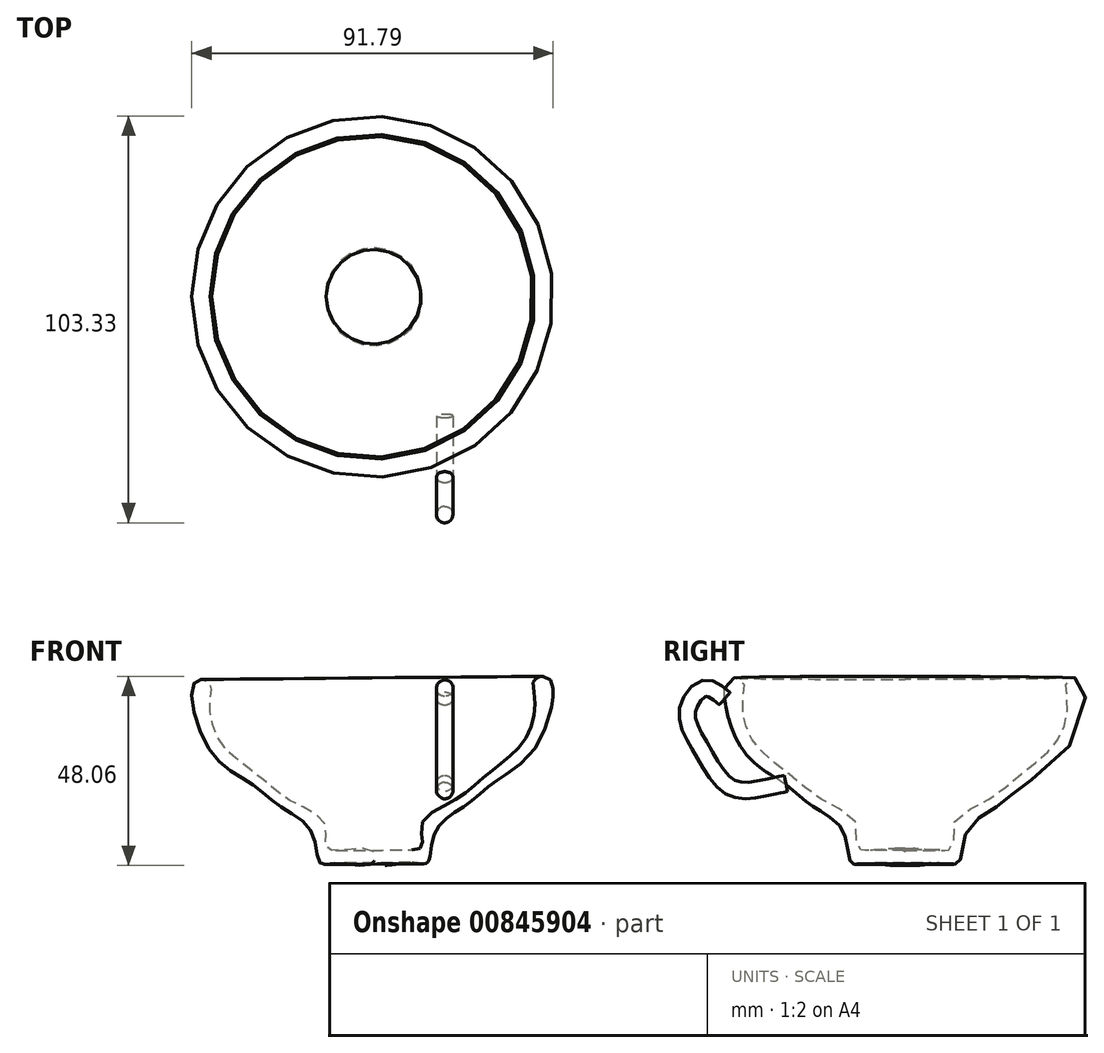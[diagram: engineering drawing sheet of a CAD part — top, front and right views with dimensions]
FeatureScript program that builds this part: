
annotation { "Feature Type Name" : "Feature", "Feature Type Description" : "" }
export const myFeature = defineFeature(function(context is Context, id is Id, definition is map)
    precondition{}
    {
        {
            var Q0;
            Q0=qCreatedBy(makeId("Front.planeOp"),FACE);
            var sketch = newSketch(context, id + "F0", { "sketchPlane" : qUnion([Q0])});
            skFitSpline(sketch, "E0", {"points": [v(-63.87, 46.09) * mm, v(-60.42, 29.17) * mm, v(-49.71, 20.2) * mm, v(-42.12, 14.33) * mm, v(-34.18, 7.77) * mm, v(-32.1, 0) * mm, v(-27.96, 0) * mm, v(-18.99, 0) * mm, v(-18.99, 3.28) * mm, v(-30.38, 3.62) * mm, v(-30.73, 9.5) * mm, v(-39.36, 15.7) * mm, v(-46.26, 20.89) * mm, v(-52.48, 25.72) * mm, v(-58.34, 32.28) * mm, v(-60.07, 41.6) * mm, v(-60.07, 45.74) * mm, v(-63.87, 46.09) * mm]});
            skLineSegment(sketch, "E1", {"start": v(-18.3, -18.12) * mm, "end": v(-18.99, 56.1) * mm});
            skSolve(sketch);
        }
        {
            var Q0;
            {var subQ0=sQuery(id+"F0.wireOp",EDGE,"E1");var subQ1=sQuery(id+"F0.wireOp",EDGE,"E0");var subQ2=makeQuery(id+"F0.imprint","INTERSECT",VERTEX,{"disambiguationData":[OD(0.0)],"derivedFrom":[subQ1,subQ0]});Q0=makeQuery(id+"F0.imprint","IMPRINT",FACE,{"disambiguationData":[TD([[makeQuery(id+"F0.imprint","IMPRINT",EDGE,{"disambiguationData":[TD([[subQ2,1.0]])],"derivedFrom":subQ1}),1.0]])]});}
            var Q1;
            Q1=sQuery(id+"F0.wireOp",EDGE,"E1");
            revolve(context, id + "F1", {"surfaceOperationType" : NewSurfaceOperationType.NEW, "entities" : qUnion([Q0]), "axis" : qUnion([Q1]), "revolveType" : RevolveType.FULL});
        }
        {
            var Q0;
            Q0=qCreatedBy(makeId("Right.planeOp"),FACE);
            var sketch = newSketch(context, id + "F2", { "sketchPlane" : qUnion([Q0])});
            skFitSpline(sketch, "E2", {"points": [v(-45.5, 42.18) * mm, v(-50.98, 44.92) * mm, v(-55.78, 38.75) * mm, v(-52.12, 28.69) * mm, v(-44.12, 18.63) * mm, v(-34.52, 18.86) * mm, v(-30.18, 19.77) * mm], "startDerivative": vector(-37.73, 32.86) * mm, "endDerivative": vector(31.08, 6.22) * mm});
            skSolve(sketch);
        }
        {
            var Q0;
            Q0=sQuery(id+"F2.wireOp",EDGE,"E2");
            var Q1;
            Q1=sQuery(id+"F2.wireOp",VERTEX,"E2.end");
            cPlane(context, id + "F3", {"entities" : qUnion([Q0, Q1]), "cplaneType" : CPlaneType.CURVE_POINT, "offset" : 25.4 * mm, "width" : 152.4 * mm, "height" : 152.4 * mm});
        }
        {
            var Q0;
            Q0=qCreatedBy(id+"F3.planeOp",FACE);
            var sketch = newSketch(context, id + "F4", { "sketchPlane" : qUnion([Q0])});
            skCircle(sketch, "E3", {"center": v(0.48, 25.81) * mm, "radius": 2.09 * mm});
            skSolve(sketch);
        }
        {
            var Q0;
            Q0=makeQuery(id+"F4.imprint","IMPRINT",FACE,{"disambiguationData":[TD([[makeQuery(id+"F4.imprint","IMPRINT",EDGE,{"derivedFrom":sQuery(id+"F4.wireOp",EDGE,"E3")}),1.0]])]});
            var Q1;
            Q1=sQuery(id+"F2.wireOp",EDGE,"E2");
            sweep(context, id + "F5", {"profiles" : qUnion([Q0]), "path" : qUnion([Q1])});
        }
    });
